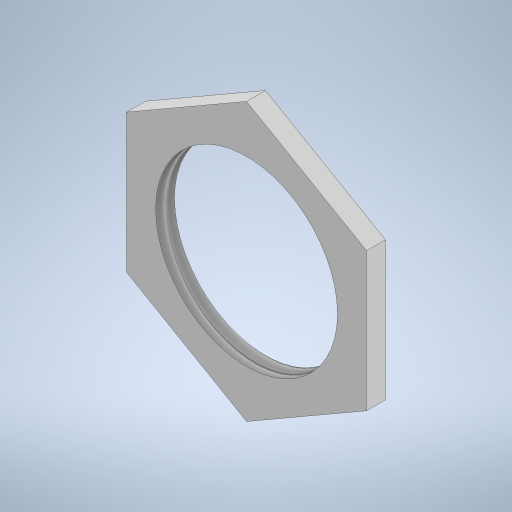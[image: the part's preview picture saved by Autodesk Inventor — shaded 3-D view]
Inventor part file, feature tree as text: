
AUTODESK INVENTOR PART (.ipt)
format: ipt  version: 2023 (Build 270158000, 158)  size: 242,176 bytes
history: native  units: in
note: dims shown in document units (in); Inventor stores cm internally (conversion verified against a paired STEP export)
features: sketch x2, extrude x1, hole x1
ambient origin geometry x8: Origin, YZ Plane, XZ Plane, XY Plane, X Axis, Y Axis, Z Axis, Center Point
bodies: Solid1 (feature_tree)
feature tree (4):
  extrude  "Extrusion1"  Depth=0.0787in TaperAngle=0.0deg
  hole  "Hole1"  [1 undecoded]
  sketch  "Sketch1"  dims[d0=1.0in d1=0.0787in d2=0.0in]
  sketch  "Sketch2"  dims[d3=0.758in d4=1.625in d5=0.1575in d6=0.0787in d7=90.0deg d8=0.315in d9=0.8108in]
note: 1 required parameter value undecoded (feature->parameter linkage not recoverable at this tier; creation-order binding heuristic only, values carry confidence <= 0.55)
